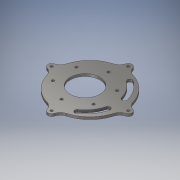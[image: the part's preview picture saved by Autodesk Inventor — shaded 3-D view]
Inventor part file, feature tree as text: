
AUTODESK INVENTOR PART (.ipt)
format: ipt  version: 2019 (Build 230136000, 136)  size: 213,504 bytes
history: native  units: in
note: dims shown in document units (in); Inventor stores cm internally (conversion verified against a paired STEP export)
features: sketch x4, extrude x2, hole x2, projected_geometry x1
ambient origin geometry x8: Origin, YZ Plane, XZ Plane, XY Plane, X Axis, Y Axis, Z Axis, Center Point
bodies: Solid1 (feature_tree)
feature tree (9):
  extrude  "Extrusion1"  Depth=3.0in
  hole  "Hole1"  [1 undecoded]
  hole  "Hole2"  [1 undecoded]
  extrude  "Extrusion3"  Depth=0.5in
  sketch  "Sketch1"  dims[d0=3.0in d2=0.75in]
  sketch  "Sketch3"  dims[d3=0.9in d4=0.25in d5=0.0in]
  sketch  "Sketch6"  dims[d10=0.257in d11=0.75in d12=0.438in d13=0.25in d14=0.5635in d15=0.484in d16=0.8108in d20=7.0in]
  sketch  "Sketch8"  dims[d21=0.5in d22=3.937in d25=2.3622in d27=360.0deg d29=0.257in d30=0.75in d31=0.438in d32=0.25in d33=0.5635in d34=0.484in d35=0.8108in d36=5.5in d37=0.375in d38=1.5in d39=0.5in d40=0.3779in d41=0.3779in d42=0.2749in d43=0.2749in d44=1.0in d45=0.0in]
  projected_geometry  "Project Cut Edges2"
note: 2 required parameter values undecoded (feature->parameter linkage not recoverable at this tier; creation-order binding heuristic only, values carry confidence <= 0.55)
